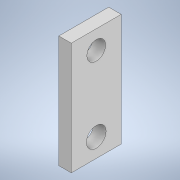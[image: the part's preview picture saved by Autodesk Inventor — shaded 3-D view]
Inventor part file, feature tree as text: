
AUTODESK INVENTOR PART (.ipt)
format: ipt  version: 2021 (Build 250183000, 183)  size: 111,104 bytes
history: native  units: mm
features: extrude x3, sketch x3
ambient origin geometry x8: Origin, YZ Plane, XZ Plane, XY Plane, X Axis, Y Axis, Z Axis, Center Point
bodies: Solid1 (feature_tree)
feature tree (6):
  extrude  "Extrusion1"  Depth=40.0mm
  extrude  "Extrusion2"  Depth=10.0mm
  extrude  "Extrusion3"  Depth=15.0mm
  sketch  "Sketch1"  dims[d0=90.0mm d1=40.0mm]
  sketch  "Sketch2"  dims[d2=10.0mm d3=0.0mm d4=15.0mm]
  sketch  "Sketch3"  dims[d5=50.0mm d6=0.0mm d7=15.0mm d8=15.0mm d9=50.0mm d10=0.0mm]
